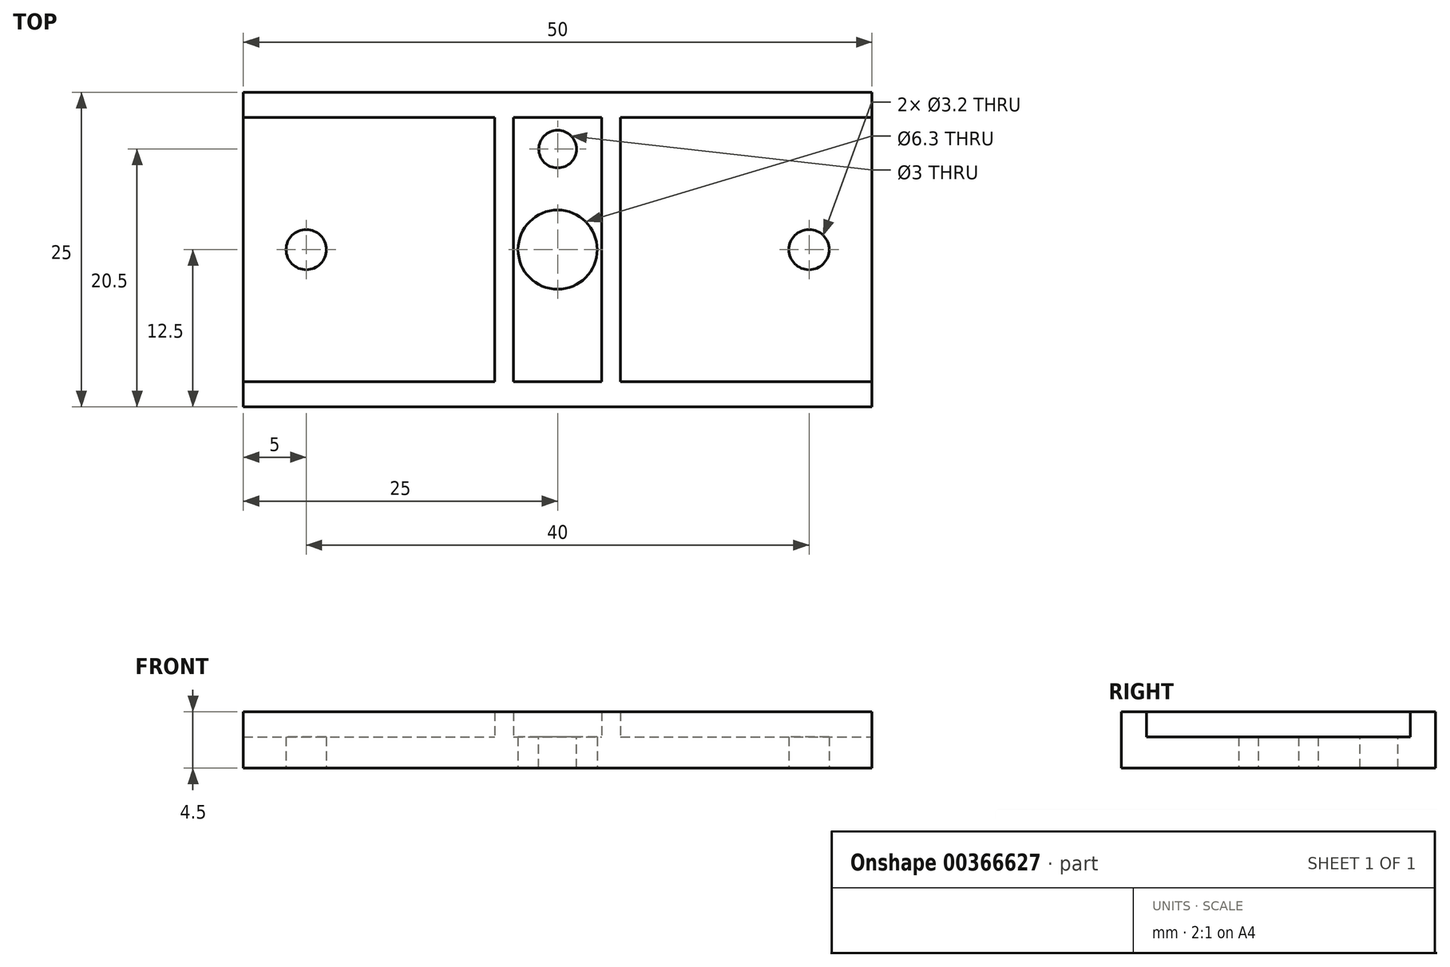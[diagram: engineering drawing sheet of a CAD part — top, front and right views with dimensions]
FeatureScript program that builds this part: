
annotation { "Feature Type Name" : "Feature", "Feature Type Description" : "" }
export const myFeature = defineFeature(function(context is Context, id is Id, definition is map)
    precondition{}
    {
        {
            var Q0;
            Q0=qCreatedBy(makeId("Top.planeOp"),FACE);
            var sketch = newSketch(context, id + "F0", { "sketchPlane" : qUnion([Q0])});
            skLineSegment(sketch, "E0.bottom", {"start": v(25, -12.5) * mm, "end": v(-25, -12.5) * mm});
            skLineSegment(sketch, "E0.top", {"start": v(25, 12.5) * mm, "end": v(-25, 12.5) * mm});
            skLineSegment(sketch, "E0.left", {"start": v(25, -12.5) * mm, "end": v(25, 12.5) * mm});
            skLineSegment(sketch, "E0.right", {"start": v(-25, -12.5) * mm, "end": v(-25, 12.5) * mm});
            skPoint(sketch, "E0.middle", {"position": v(0, 0) * mm});
            skCircle(sketch, "E1", {"center": v(-20, 0) * mm, "radius": 1.6 * mm});
            skCircle(sketch, "E2", {"center": v(20, 0) * mm, "radius": 1.6 * mm});
            skCircle(sketch, "E3", {"center": v(0, 0) * mm, "radius": 3.15 * mm});
            skSolve(sketch);
        }
        {
            var Q0;
            Q0 = qSketchRegion(id + "F0", true);
            extrude(context, id + "F1", {"entities" : qUnion([Q0]), "depth" : 2.5 * mm});
        }
        {
            var Q0;
            Q0=makeQuery(id+"F1.opExtrude","CAP_FACE",FACE,{"disambiguationData":[OSD([sQuery(id+"F0.wireOp",EDGE,"E0.bottom"),sQuery(id+"F0.wireOp",EDGE,"E0.top"),sQuery(id+"F0.wireOp",EDGE,"E0.left"),sQuery(id+"F0.wireOp",EDGE,"E0.right"),sQuery(id+"F0.wireOp",EDGE,"E1"),sQuery(id+"F0.wireOp",EDGE,"E2"),sQuery(id+"F0.wireOp",EDGE,"E3")])],"isStart":false});
            var sketch = newSketch(context, id + "F2", { "sketchPlane" : qUnion([Q0])});
            skCircle(sketch, "E4", {"center": v(0, 8) * mm, "radius": 1.5 * mm});
            skSolve(sketch);
        }
        {
            var Q0;
            Q0 = qSketchRegion(id + "F2", true);
            extrude(context, id + "F3", {"entities" : qUnion([Q0]), "operationType" : NewBodyOperationType.REMOVE, "oppositeDirection" : true, "depth" : 25 * mm});
        }
        {
            var Q0;
            Q0=makeQuery(id+"F1.opExtrude","CAP_FACE",FACE,{"disambiguationData":[OSD([sQuery(id+"F0.wireOp",EDGE,"E0.bottom"),sQuery(id+"F0.wireOp",EDGE,"E0.top"),sQuery(id+"F0.wireOp",EDGE,"E0.left"),sQuery(id+"F0.wireOp",EDGE,"E0.right"),sQuery(id+"F0.wireOp",EDGE,"E1"),sQuery(id+"F0.wireOp",EDGE,"E2"),sQuery(id+"F0.wireOp",EDGE,"E3")])],"isStart":false});
            var sketch = newSketch(context, id + "F4", { "sketchPlane" : qUnion([Q0])});
            skLineSegment(sketch, "E5.bottom", {"start": v(-25, 12.5) * mm, "end": v(25, 12.5) * mm});
            skLineSegment(sketch, "E5.top", {"start": v(-25, 10.5) * mm, "end": v(25, 10.5) * mm});
            skLineSegment(sketch, "E5.left", {"start": v(-25, 12.5) * mm, "end": v(-25, 10.5) * mm});
            skLineSegment(sketch, "E5.right", {"start": v(25, 12.5) * mm, "end": v(25, 10.5) * mm});
            skLineSegment(sketch, "E6.bottom", {"start": v(-25, -12.5) * mm, "end": v(25, -12.5) * mm});
            skLineSegment(sketch, "E6.top", {"start": v(-25, -10.5) * mm, "end": v(25, -10.5) * mm});
            skLineSegment(sketch, "E6.left", {"start": v(-25, -12.5) * mm, "end": v(-25, -10.5) * mm});
            skLineSegment(sketch, "E6.right", {"start": v(25, -12.5) * mm, "end": v(25, -10.5) * mm});
            skLineSegment(sketch, "E7.bottom", {"start": v(-3.5, 10.5) * mm, "end": v(-5, 10.5) * mm});
            skLineSegment(sketch, "E7.top", {"start": v(-3.5, -10.5) * mm, "end": v(-5, -10.5) * mm});
            skLineSegment(sketch, "E7.left", {"start": v(-3.5, 10.5) * mm, "end": v(-3.5, -10.5) * mm});
            skLineSegment(sketch, "E7.right", {"start": v(-5, 10.5) * mm, "end": v(-5, -10.5) * mm});
            skLineSegment(sketch, "E8.bottom", {"start": v(5, 10.5) * mm, "end": v(3.5, 10.5) * mm});
            skLineSegment(sketch, "E8.top", {"start": v(5, -10.5) * mm, "end": v(3.5, -10.5) * mm});
            skLineSegment(sketch, "E8.left", {"start": v(5, 10.5) * mm, "end": v(5, -10.5) * mm});
            skLineSegment(sketch, "E8.right", {"start": v(3.5, 10.5) * mm, "end": v(3.5, -10.5) * mm});
            skSolve(sketch);
        }
        {
            var Q0;
            Q0 = qSketchRegion(id + "F4", true);
            extrude(context, id + "F5", {"entities" : qUnion([Q0]), "operationType" : NewBodyOperationType.ADD, "depth" : 2 * mm});
        }
    });
